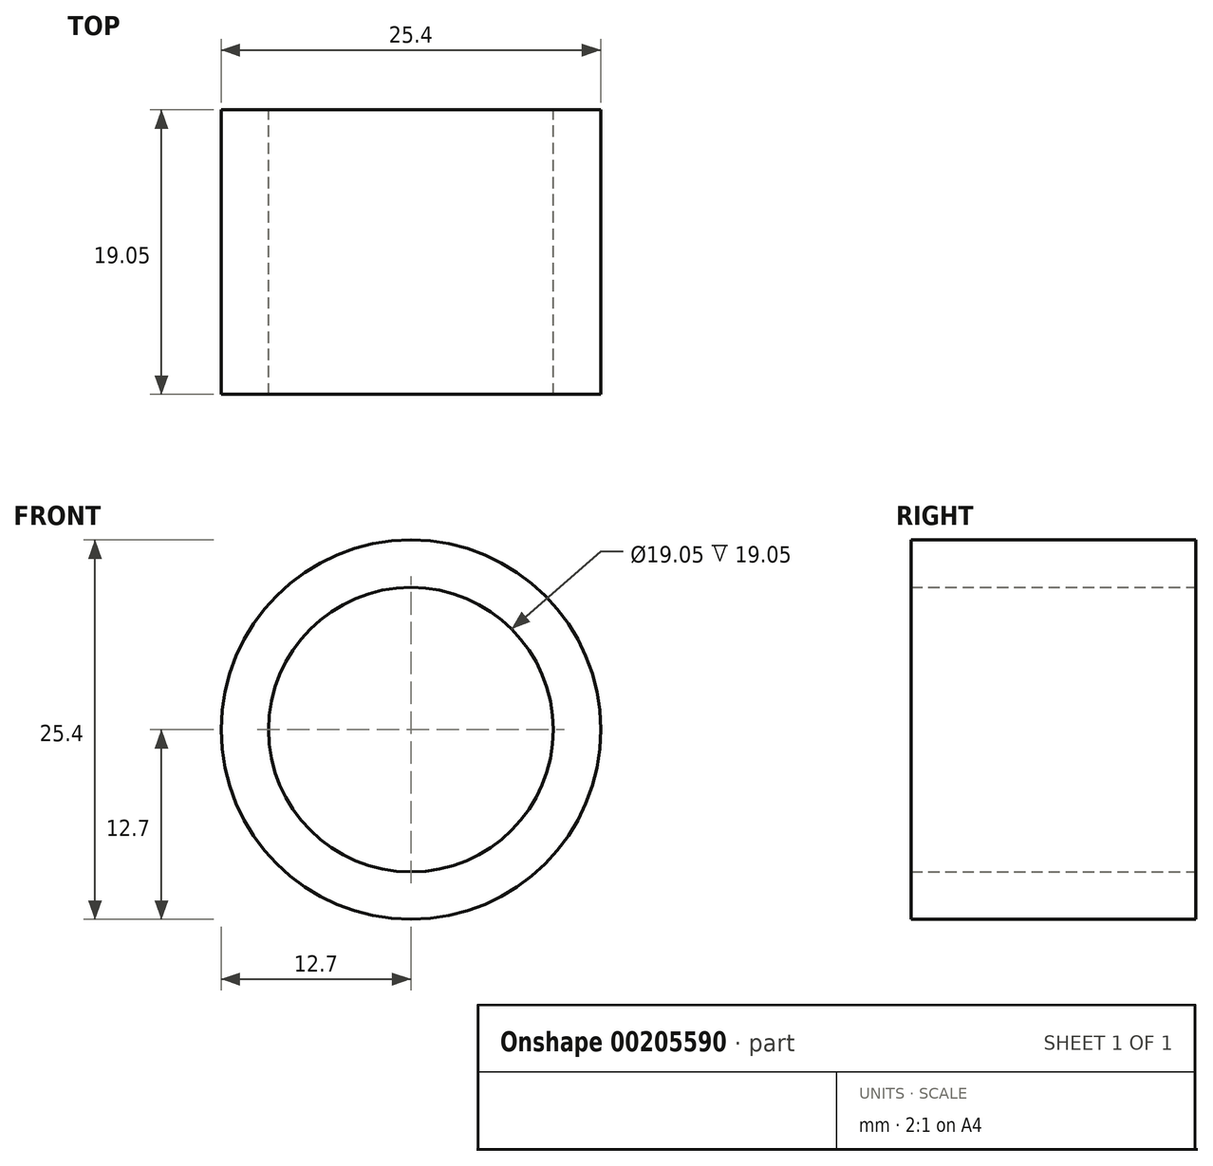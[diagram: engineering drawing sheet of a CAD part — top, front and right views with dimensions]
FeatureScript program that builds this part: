
annotation { "Feature Type Name" : "Feature", "Feature Type Description" : "" }
export const myFeature = defineFeature(function(context is Context, id is Id, definition is map)
    precondition{}
    {
        {
            var Q0;
            Q0=qCreatedBy(makeId("Front.planeOp"),FACE);
            var sketch = newSketch(context, id + "F0", { "sketchPlane" : qUnion([Q0])});
            skCircle(sketch, "E0", {"center": v(0, 0) * mm, "radius": 9.53 * mm});
            skCircle(sketch, "E1", {"center": v(0, 0) * mm, "radius": 12.7 * mm});
            skSolve(sketch);
        }
        {
            var Q0;
            Q0=qSketchRegion(id+"F0",true);
            extrude(context, id + "F1", {"entities" : qUnion([Q0]), "depth" : 19.05 * mm});
        }
    });
